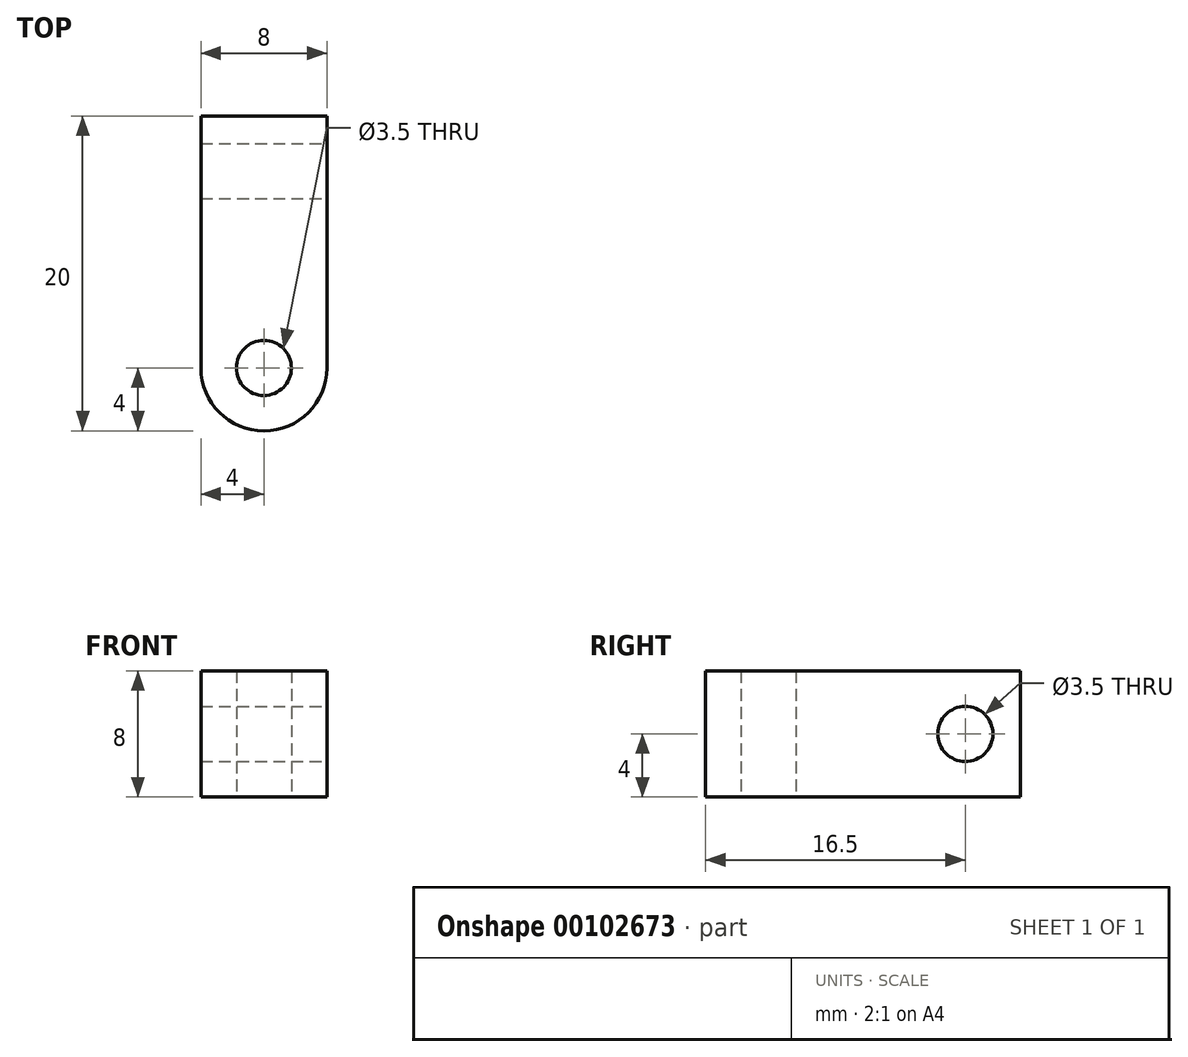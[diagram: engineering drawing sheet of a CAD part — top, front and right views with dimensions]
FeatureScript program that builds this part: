
annotation { "Feature Type Name" : "Feature", "Feature Type Description" : "" }
export const myFeature = defineFeature(function(context is Context, id is Id, definition is map)
    precondition{}
    {
        {
            var Q0;
            Q0=qCreatedBy(makeId("Top.planeOp"),FACE);
            var sketch = newSketch(context, id + "F0", { "sketchPlane" : qUnion([Q0])});
            skCircle(sketch, "E0", {"center": v(0, 0) * mm, "radius": 1.75 * mm});
            skArc(sketch, "E1", {"start": v(-4, 0) * mm, "mid": v(0, -4) * mm, "end": v(4, 0) * mm});
            skLineSegment(sketch, "E2", {"start": v(-4, 0) * mm, "end": v(-4, 16) * mm});
            skLineSegment(sketch, "E3", {"start": v(-4, 16) * mm, "end": v(4, 16) * mm});
            skLineSegment(sketch, "E4", {"start": v(4, 16) * mm, "end": v(4, 0) * mm});
            skSolve(sketch);
        }
        {
            var Q0;
            Q0=makeQuery(id+"F0.imprint","IMPRINT",FACE,{"disambiguationData":[TD([[makeQuery(id+"F0.imprint","IMPRINT",EDGE,{"derivedFrom":sQuery(id+"F0.wireOp",EDGE,"E0")}),-1.0]])]});
            extrude(context, id + "F1", {"entities" : qUnion([Q0]), "depth" : 8 * mm});
        }
        {
            var Q0;
            Q0=makeQuery(id+"F1.opExtrude","SWEPT_FACE",FACE,{"disambiguationData":[OSD([sQuery(id+"F0.wireOp",EDGE,"E4")])]});
            var sketch = newSketch(context, id + "F2", { "sketchPlane" : qUnion([Q0])});
            skPoint(sketch, "E5.centerSnap0", {"position": v(16, 4) * mm});
            skPoint(sketch, "E5.centerSnap1", {"position": v(8, 8) * mm});
            skCircle(sketch, "E6", {"center": v(12.5, 4) * mm, "radius": 1.75 * mm});
            skSolve(sketch);
        }
        {
            var Q0;
            Q0=makeQuery(id+"F2.imprint","IMPRINT",FACE,{"disambiguationData":[TD([[makeQuery(id+"F2.imprint","IMPRINT",EDGE,{"derivedFrom":sQuery(id+"F2.wireOp",EDGE,"E6")}),1.0]])]});
            extrude(context, id + "F3", {"entities" : qUnion([Q0]), "operationType" : NewBodyOperationType.REMOVE, "oppositeDirection" : true, "depth" : 20 * mm});
        }
    });
